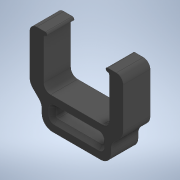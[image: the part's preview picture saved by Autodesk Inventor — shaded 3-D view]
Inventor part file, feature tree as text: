
AUTODESK INVENTOR PART (.ipt)
format: ipt  version: 2021.5 (Build 255421000, 421)  size: 178,176 bytes
history: native  units: mm
features: fillet x2, chamfer x2, other x1, extrude x1, sketch x1
ambient origin geometry x8: Origin, YZ Plane, XZ Plane, XY Plane, X Axis, Y Axis, Z Axis, Center Point
bodies: Body1 (feature_tree)
feature tree (7):
  other  "Sólido1"
  extrude  "Extrusión1"  Depth=3.0mm
  fillet  "Empalme1"  Radius=3.0mm
  chamfer  "Chaflán2"  Distance=9.5mm
  chamfer  "Chaflán1"  Distance=4.0mm
  fillet  "Empalme2"  Radius=14.0mm
  sketch  "Boceto1"  dims[d0=14.0mm d1=3.0mm d2=3.0mm d3=9.5mm d4=4.0mm d5=14.0mm d6=7.8mm d7=0.0mm d8=5.0mm d9=1.0mm d10=0.5mm d12=3.0mm d13=2.0mm d14=1.0mm d15=2.0mm d16=45.0deg d17=3.5mm d18=2.0mm d19=45.0deg d20=3.0mm]
